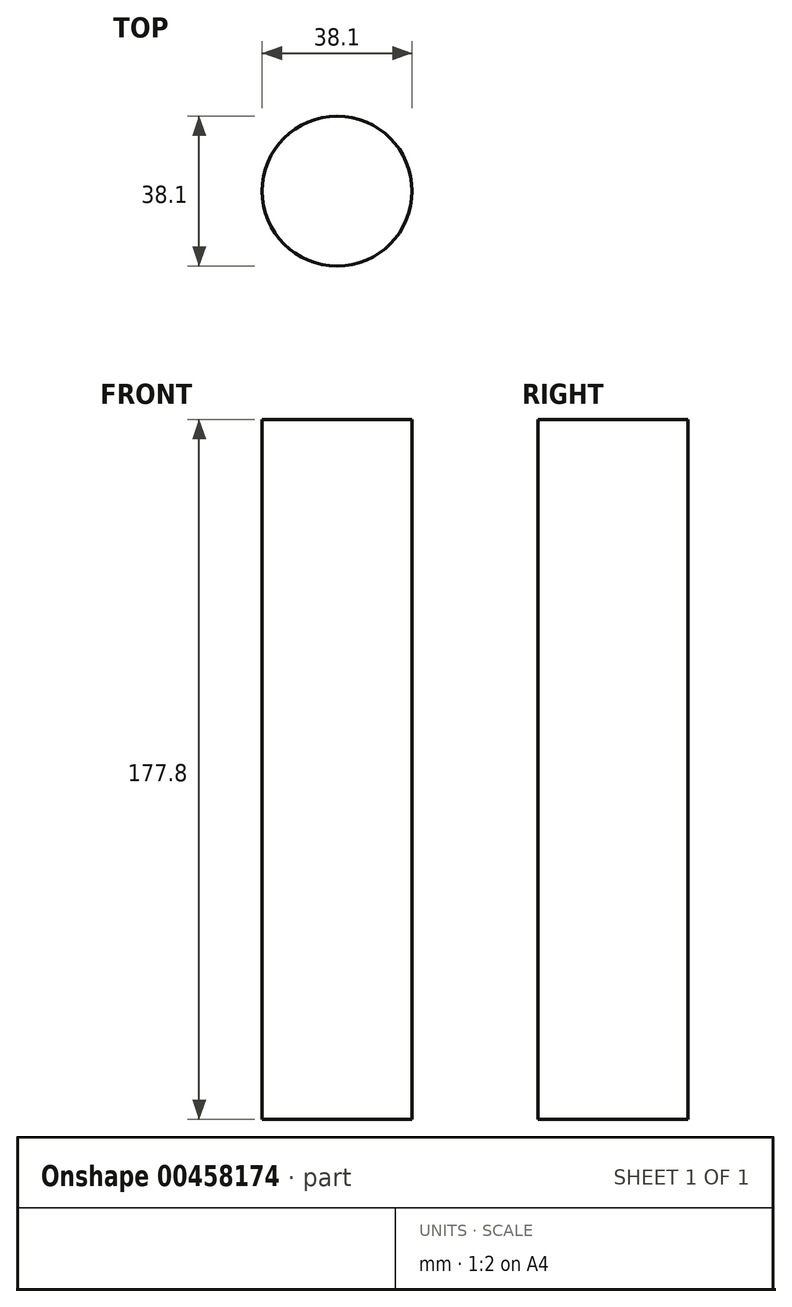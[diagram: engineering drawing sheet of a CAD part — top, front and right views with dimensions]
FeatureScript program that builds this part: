
annotation { "Feature Type Name" : "Feature", "Feature Type Description" : "" }
export const myFeature = defineFeature(function(context is Context, id is Id, definition is map)
    precondition{}
    {
        {
            var Q0;
            Q0=qCreatedBy(makeId("Front.planeOp"),FACE);
            var sketch = newSketch(context, id + "F0", { "sketchPlane" : qUnion([Q0])});
            skLineSegment(sketch, "E0.bottom", {"start": v(0, -84.94) * mm, "end": v(19.05, -84.94) * mm});
            skLineSegment(sketch, "E0.top", {"start": v(0, 92.86) * mm, "end": v(19.05, 92.86) * mm});
            skLineSegment(sketch, "E0.left", {"start": v(0, -84.94) * mm, "end": v(0, 92.86) * mm});
            skLineSegment(sketch, "E0.right", {"start": v(19.05, -84.94) * mm, "end": v(19.05, 92.86) * mm});
            skSolve(sketch);
        }
        {
            var Q0;
            Q0=makeQuery(id+"F0.imprint","IMPRINT",FACE,{"disambiguationData":[TD([[makeQuery(id+"F0.imprint","IMPRINT",EDGE,{"derivedFrom":sQuery(id+"F0.wireOp",EDGE,"E0.bottom")}),1.0]])]});
            var Q1;
            Q1=sQuery(id+"F0.wireOp",EDGE,"E0.left");
            revolve(context, id + "F1", {"entities" : qUnion([Q0]), "axis" : qUnion([Q1]), "revolveType" : RevolveType.FULL});
        }
    });
